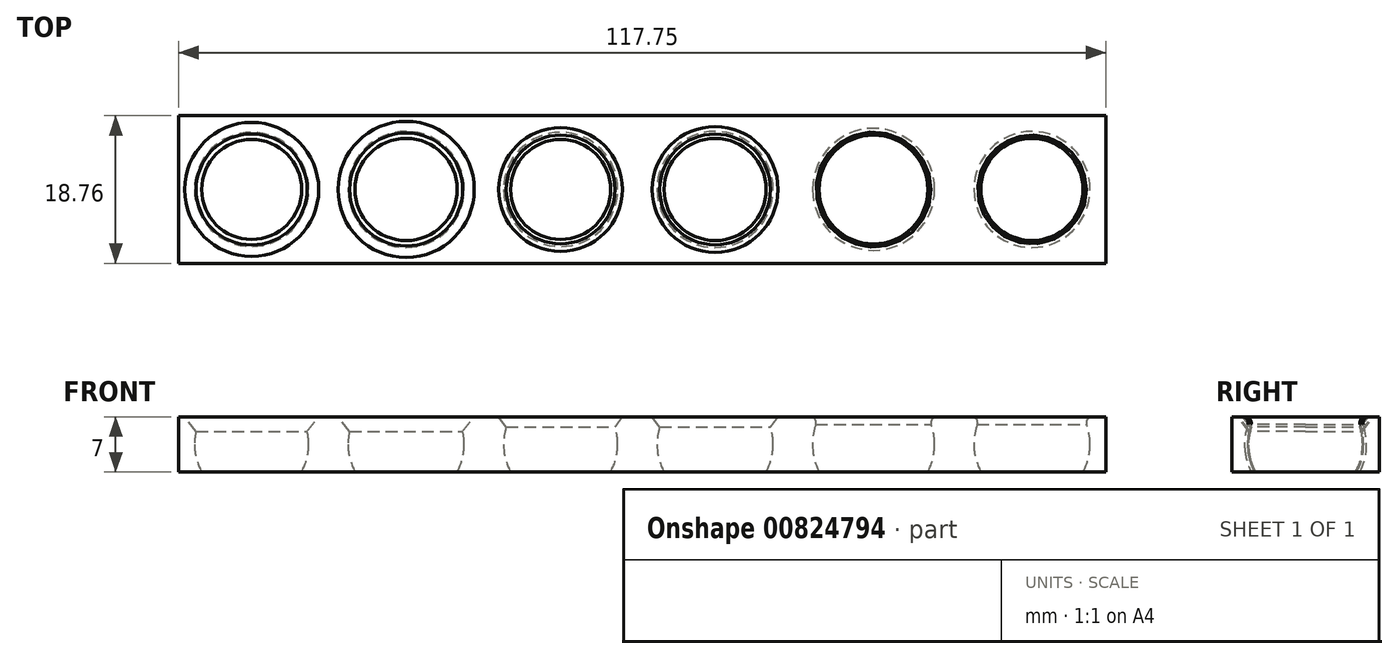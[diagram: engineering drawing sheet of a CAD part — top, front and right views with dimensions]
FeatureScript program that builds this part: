
annotation { "Feature Type Name" : "Feature", "Feature Type Description" : "" }
export const myFeature = defineFeature(function(context is Context, id is Id, definition is map)
    precondition{}
    {
        {
            var Q0;
            Q0=qCreatedBy(makeId("Top.planeOp"),FACE);
            var sketch = newSketch(context, id + "F0", { "sketchPlane" : qUnion([Q0])});
            skLineSegment(sketch, "E0", {"start": v(-79.24, 0) * mm, "end": v(83.97, 0) * mm, "construction": true});
            skArc(sketch, "E1", {"start": v(-47.78, 0) * mm, "mid": v(-55.03, 7.25) * mm, "end": v(-62.28, 0) * mm});
            skArc(sketch, "E2", {"start": v(-28.03, 0) * mm, "mid": v(-35.4, 7.38) * mm, "end": v(-42.78, 0) * mm});
            skArc(sketch, "E3", {"start": v(-8.53, 0) * mm, "mid": v(-15.78, 7.25) * mm, "end": v(-23.03, 0) * mm});
            skArc(sketch, "E4", {"start": v(11.22, 0) * mm, "mid": v(3.85, 7.38) * mm, "end": v(-3.53, 0) * mm});
            skArc(sketch, "E5", {"start": v(31.72, 0) * mm, "mid": v(23.97, 7.75) * mm, "end": v(16.22, 0) * mm});
            skArc(sketch, "E6", {"start": v(51.47, 0) * mm, "mid": v(44.1, 7.38) * mm, "end": v(36.72, 0) * mm});
            skLineSegment(sketch, "E7", {"start": v(-62.28, 0) * mm, "end": v(-47.78, 0) * mm});
            skLineSegment(sketch, "E8", {"start": v(-42.78, 0) * mm, "end": v(-28.03, 0) * mm});
            skLineSegment(sketch, "E9", {"start": v(-23.03, 0) * mm, "end": v(-8.53, 0) * mm});
            skLineSegment(sketch, "E10", {"start": v(-3.53, 0) * mm, "end": v(11.22, 0) * mm});
            skLineSegment(sketch, "E11", {"start": v(16.22, 0) * mm, "end": v(31.72, 0) * mm});
            skLineSegment(sketch, "E12", {"start": v(36.72, 0) * mm, "end": v(51.47, 0) * mm});
            skLineSegment(sketch, "E13.bottom", {"start": v(-64.28, 9.38) * mm, "end": v(53.47, 9.38) * mm});
            skLineSegment(sketch, "E13.top", {"start": v(-64.28, -9.38) * mm, "end": v(53.47, -9.38) * mm});
            skLineSegment(sketch, "E13.left", {"start": v(-64.28, 9.38) * mm, "end": v(-64.28, -9.38) * mm});
            skLineSegment(sketch, "E13.right", {"start": v(53.47, 9.38) * mm, "end": v(53.47, -9.38) * mm});
            skSolve(sketch);
        }
        {
            var Q0;
            Q0=makeQuery(id+"F0.imprint","IMPRINT",FACE,{"disambiguationData":[TD([[makeQuery(id+"F0.imprint","IMPRINT",EDGE,{"derivedFrom":sQuery(id+"F0.wireOp",EDGE,"E1")}),-1.0]])]});
            var Q1;
            Q1=makeQuery(id+"F0.imprint","IMPRINT",FACE,{"disambiguationData":[TD([[makeQuery(id+"F0.imprint","IMPRINT",EDGE,{"derivedFrom":sQuery(id+"F0.wireOp",EDGE,"E1")}),1.0]])]});
            var Q2;
            Q2=makeQuery(id+"F0.imprint","IMPRINT",FACE,{"disambiguationData":[TD([[makeQuery(id+"F0.imprint","IMPRINT",EDGE,{"derivedFrom":sQuery(id+"F0.wireOp",EDGE,"E2")}),1.0]])]});
            var Q3;
            Q3=makeQuery(id+"F0.imprint","IMPRINT",FACE,{"disambiguationData":[TD([[makeQuery(id+"F0.imprint","IMPRINT",EDGE,{"derivedFrom":sQuery(id+"F0.wireOp",EDGE,"E3")}),1.0]])]});
            var Q4;
            Q4=makeQuery(id+"F0.imprint","IMPRINT",FACE,{"disambiguationData":[TD([[makeQuery(id+"F0.imprint","IMPRINT",EDGE,{"derivedFrom":sQuery(id+"F0.wireOp",EDGE,"E4")}),1.0]])]});
            var Q5;
            Q5=makeQuery(id+"F0.imprint","IMPRINT",FACE,{"disambiguationData":[TD([[makeQuery(id+"F0.imprint","IMPRINT",EDGE,{"derivedFrom":sQuery(id+"F0.wireOp",EDGE,"E5")}),1.0]])]});
            var Q6;
            Q6=makeQuery(id+"F0.imprint","IMPRINT",FACE,{"disambiguationData":[TD([[makeQuery(id+"F0.imprint","IMPRINT",EDGE,{"derivedFrom":sQuery(id+"F0.wireOp",EDGE,"E6")}),1.0]])]});
            extrude(context, id + "F1", {"entities" : qUnion([Q0, Q1, Q2, Q3, Q4, Q5, Q6]), "endBound" : BoundingType.SYMMETRIC, "depth" : 7 * mm, "offsetDistance" : 25 * mm});
        }
        {
            var Q0;
            Q0=makeQuery(id+"F0.imprint","IMPRINT",FACE,{"disambiguationData":[TD([[makeQuery(id+"F0.imprint","IMPRINT",EDGE,{"derivedFrom":sQuery(id+"F0.wireOp",EDGE,"E1")}),1.0]])]});
            var Q1;
            Q1=makeQuery(id+"F0.imprint","IMPRINT",FACE,{"disambiguationData":[TD([[makeQuery(id+"F0.imprint","IMPRINT",EDGE,{"derivedFrom":sQuery(id+"F0.wireOp",EDGE,"E2")}),1.0]])]});
            var Q2;
            Q2=makeQuery(id+"F0.imprint","IMPRINT",FACE,{"disambiguationData":[TD([[makeQuery(id+"F0.imprint","IMPRINT",EDGE,{"derivedFrom":sQuery(id+"F0.wireOp",EDGE,"E3")}),1.0]])]});
            var Q3;
            Q3=makeQuery(id+"F0.imprint","IMPRINT",FACE,{"disambiguationData":[TD([[makeQuery(id+"F0.imprint","IMPRINT",EDGE,{"derivedFrom":sQuery(id+"F0.wireOp",EDGE,"E4")}),1.0]])]});
            var Q4;
            Q4=makeQuery(id+"F0.imprint","IMPRINT",FACE,{"disambiguationData":[TD([[makeQuery(id+"F0.imprint","IMPRINT",EDGE,{"derivedFrom":sQuery(id+"F0.wireOp",EDGE,"E5")}),1.0]])]});
            var Q5;
            Q5=makeQuery(id+"F0.imprint","IMPRINT",FACE,{"disambiguationData":[TD([[makeQuery(id+"F0.imprint","IMPRINT",EDGE,{"derivedFrom":sQuery(id+"F0.wireOp",EDGE,"E6")}),1.0]])]});
            var Q6;
            Q6=sQuery(id+"F0.wireOp",EDGE,"E0");
            revolve(context, id + "F2", {"operationType" : NewBodyOperationType.REMOVE, "surfaceOperationType" : NewSurfaceOperationType.NEW, "entities" : qUnion([Q0, Q1, Q2, Q3, Q4, Q5]), "axis" : qUnion([Q6]), "revolveType" : RevolveType.FULL, "oppositeDirection" : true});
        }
        {
            var Q0;
            Q0=makeQuery(id+"F2.boolean.opBoolean","INTERSECT",EDGE,{"derivedFrom":[makeQuery(id+"F1.opExtrude","CAP_FACE",FACE,{"disambiguationData":[OSD([sQuery(id+"F0.wireOp",EDGE,"E13.bottom"),sQuery(id+"F0.wireOp",EDGE,"E13.top"),sQuery(id+"F0.wireOp",EDGE,"E13.left"),sQuery(id+"F0.wireOp",EDGE,"E13.right")])],"isStart":false}),makeQuery(id+"F2.opRevolve","SWEPT_FACE",FACE,{"disambiguationData":[OSD([sQuery(id+"F0.wireOp",EDGE,"E1")])]})]});
            var Q1;
            Q1=makeQuery(id+"F2.boolean.opBoolean","INTERSECT",EDGE,{"derivedFrom":[makeQuery(id+"F1.opExtrude","CAP_FACE",FACE,{"disambiguationData":[OSD([sQuery(id+"F0.wireOp",EDGE,"E13.bottom"),sQuery(id+"F0.wireOp",EDGE,"E13.top"),sQuery(id+"F0.wireOp",EDGE,"E13.left"),sQuery(id+"F0.wireOp",EDGE,"E13.right")])],"isStart":false}),makeQuery(id+"F2.opRevolve","SWEPT_FACE",FACE,{"disambiguationData":[OSD([sQuery(id+"F0.wireOp",EDGE,"E2")])]})]});
            chamfer(context, id + "F3", {"entities" : qUnion([Q0, Q1]), "width" : 1.5 * mm, "tangentPropagation" : true});
        }
        {
            var Q0;
            Q0=makeQuery(id+"F2.boolean.opBoolean","INTERSECT",EDGE,{"derivedFrom":[makeQuery(id+"F1.opExtrude","CAP_FACE",FACE,{"disambiguationData":[OSD([sQuery(id+"F0.wireOp",EDGE,"E13.bottom"),sQuery(id+"F0.wireOp",EDGE,"E13.top"),sQuery(id+"F0.wireOp",EDGE,"E13.left"),sQuery(id+"F0.wireOp",EDGE,"E13.right")])],"isStart":false}),makeQuery(id+"F2.opRevolve","SWEPT_FACE",FACE,{"disambiguationData":[OSD([sQuery(id+"F0.wireOp",EDGE,"E3")])]})]});
            var Q1;
            Q1=makeQuery(id+"F2.boolean.opBoolean","INTERSECT",EDGE,{"derivedFrom":[makeQuery(id+"F1.opExtrude","CAP_FACE",FACE,{"disambiguationData":[OSD([sQuery(id+"F0.wireOp",EDGE,"E13.bottom"),sQuery(id+"F0.wireOp",EDGE,"E13.top"),sQuery(id+"F0.wireOp",EDGE,"E13.left"),sQuery(id+"F0.wireOp",EDGE,"E13.right")])],"isStart":false}),makeQuery(id+"F2.opRevolve","SWEPT_FACE",FACE,{"disambiguationData":[OSD([sQuery(id+"F0.wireOp",EDGE,"E4")])]})]});
            chamfer(context, id + "F4", {"entities" : qUnion([Q0, Q1]), "width" : 1 * mm, "tangentPropagation" : true});
        }
        {
            var Q0;
            Q0=makeQuery(id+"F2.boolean.opBoolean","INTERSECT",EDGE,{"derivedFrom":[makeQuery(id+"F1.opExtrude","CAP_FACE",FACE,{"disambiguationData":[OSD([sQuery(id+"F0.wireOp",EDGE,"E13.bottom"),sQuery(id+"F0.wireOp",EDGE,"E13.top"),sQuery(id+"F0.wireOp",EDGE,"E13.left"),sQuery(id+"F0.wireOp",EDGE,"E13.right")])],"isStart":false}),makeQuery(id+"F2.opRevolve","SWEPT_FACE",FACE,{"disambiguationData":[OSD([sQuery(id+"F0.wireOp",EDGE,"E5")])]})]});
            var Q1;
            Q1=makeQuery(id+"F2.boolean.opBoolean","INTERSECT",EDGE,{"derivedFrom":[makeQuery(id+"F1.opExtrude","CAP_FACE",FACE,{"disambiguationData":[OSD([sQuery(id+"F0.wireOp",EDGE,"E13.bottom"),sQuery(id+"F0.wireOp",EDGE,"E13.top"),sQuery(id+"F0.wireOp",EDGE,"E13.left"),sQuery(id+"F0.wireOp",EDGE,"E13.right")])],"isStart":false}),makeQuery(id+"F2.opRevolve","SWEPT_FACE",FACE,{"disambiguationData":[OSD([sQuery(id+"F0.wireOp",EDGE,"E6")])]})]});
            fillet(context, id + "F5", {"entities" : qUnion([Q0, Q1]), "radius" : .75 * mm, "tangentPropagation" : true, "allowEdgeOverflow" : false});
        }
    });
